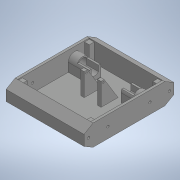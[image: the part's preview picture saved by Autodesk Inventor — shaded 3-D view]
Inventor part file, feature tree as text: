
AUTODESK INVENTOR PART (.ipt)
format: ipt  version: 2020 (Build 240168000, 168)  size: 305,152 bytes
history: native  units: in
note: dims shown in document units (in); Inventor stores cm internally (conversion verified against a paired STEP export)
features: extrude x9, sketch x9, mirror x4, projected_geometry x4, plane x1
ambient origin geometry x8: Origin, YZ Plane, XZ Plane, XY Plane, X Axis, Y Axis, Z Axis, Center Point
bodies: Solid1 (feature_tree)
feature tree (27):
  extrude  "Extrusion1"  Depth=5.9055in
  extrude  "Extrusion2"  TaperAngle=0.0deg  [1 undecoded]
  extrude  "Extrusion3"  Depth=1.2598in
  extrude  "Extrusion4"  Depth=0.315in
  extrude  "Extrusion5"  TaperAngle=0.0deg  [1 undecoded]
  extrude  "Extrusion6"  Depth=0.689in
  mirror  "Mirror1"
  extrude  "Extrusion7"  Depth=0.0787in
  mirror  "Mirror2"
  extrude  "Extrusion8"  Depth=0.5512in
  mirror  "Mirror3"
  plane  "Work Plane1"
  extrude  "Extrusion9"  Depth=0.7874in TaperAngle=0.0deg
  mirror  "Mirror4"
  sketch  "Sketch1"  dims[d0=1.378in d1=5.9055in]
  sketch  "Sketch2"  dims[d2=5.1181in d3=0.0in]
  projected_geometry  "Projected Loop1"
  sketch  "Sketch3"  dims[d4=0.1575in d5=1.2598in]
  projected_geometry  "Projected Loop2"
  projected_geometry  "Projected Loop3"
  sketch  "Sketch4"  dims[d6=0.0in d8=0.315in]
  sketch  "Sketch5"  dims[d10=1.1898in d11=0.0in]
  projected_geometry  "Projected Loop4"
  sketch  "Sketch6"  dims[d12=0.6496in d13=0.689in]
  sketch  "Sketch7"  dims[d14=1.5748in d15=0.0787in]
  sketch  "Sketch9"  dims[d16=0.5512in d17=0.0in d18=0.6102in]
  sketch  "Sketch10"  dims[d19=0.4803in d20=0.7874in d21=0.0in d22=0.1654in d23=6.063in d24=0.0in d25=0.5967in d26=0.1575in d27=1.5748in d28=0.0in d29=0.0in d30=0.1575in d31=0.2756in d32=0.0in d33=0.4331in d34=0.122in d35=0.0787in d36=0.0787in d37=0.0787in d38=2.7559in d39=0.122in d40=0.061in d41=0.0787in d42=0.2362in d43=0.0in]
note: 2 required parameter values undecoded (feature->parameter linkage not recoverable at this tier; creation-order binding heuristic only, values carry confidence <= 0.55)
